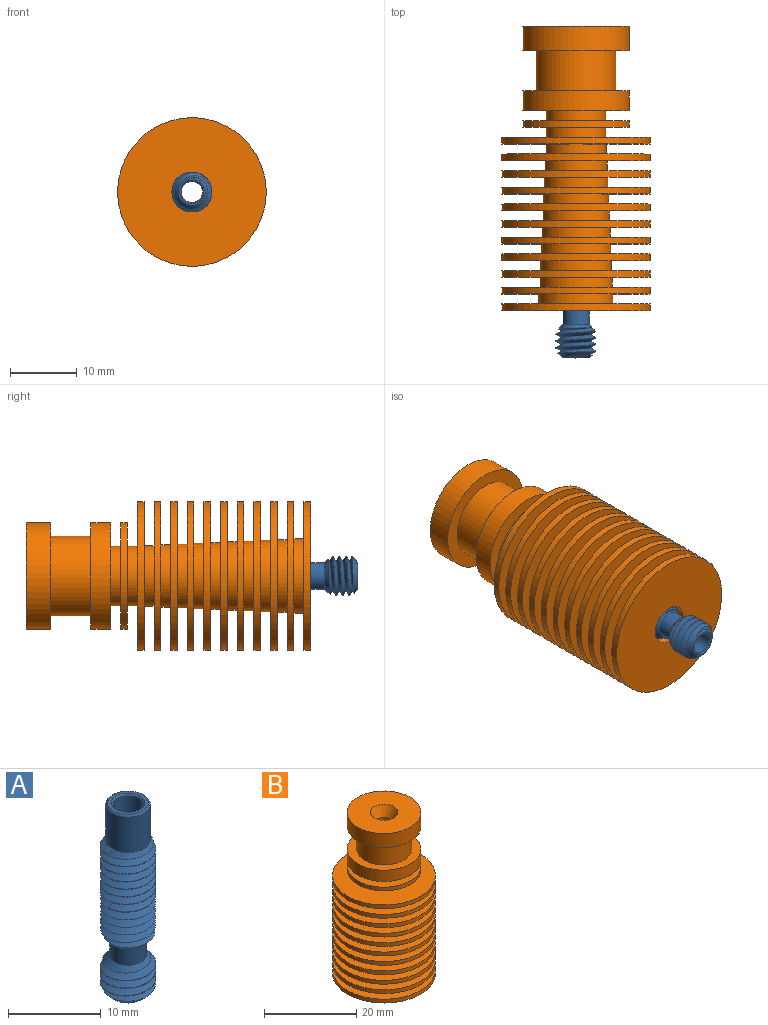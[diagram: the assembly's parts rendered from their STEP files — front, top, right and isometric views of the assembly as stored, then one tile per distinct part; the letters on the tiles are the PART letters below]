
ASSEMBLY  parts=2 mates=1
PART A: 23 faces, bbox 6x6.9x25.5 mm
  f0: cylinder r=2.4mm len=4.8mm, axis (0,0,1), area 70.9mm2, adj f11,f12,f13,f22
  f1: cylinder r=3mm len=7mm, axis (0,0,1), area 13.5mm2, adj f11,f13,f14,f17
  f2: cylinder r=3mm len=6mm, axis (0,0,1), area 4.2mm2, adj f7,f9,f18,f19
  f3: cylinder r=1.6mm len=24.7mm, axis (0,0,1), area 248.3mm2, adj f20,f21
  f4: plane 4.4x4.4mm, normal (0,0,1), area 5mm2, adj f21,f22
  f5: cylinder r=2mm len=4mm, axis (0,0,1), area 26.4mm2, adj f8,f10
  f6: plane 4x4mm, normal (0,0,-1), area 2.4mm2, adj f7,f20
  f7: cone r=3mm half-angle=45deg, axis (0,0,1), area 13.2mm2, adj f2,f6,f18,f19
  f8: cone r=2mm half-angle=45deg, axis (0,0,-1), area 13.1mm2, adj f5,f9,f18,f19
  f9: cone r=2mm half-angle=45deg, axis (0,0,-1), area 0.2mm2, adj f2,f8,f18
  f10: cone r=3mm half-angle=45deg, axis (0,0,1), area 11.5mm2, adj f5,f13,f14,f15,f16
  f11: cone r=2mm half-angle=45deg, axis (0,0,-1), area 6.7mm2, adj f0,f1,f12,f13,f14
  f12: plane 0.62x0.47mm, normal (0,1,0), area 0.1mm2, adj f0,f11,f13,f14
  f13: bspline ~13.63x6.93mm, area 182.7mm2, adj f0,f1,f10,f11,f12,f14,f16,f17
  f14: bspline ~13.46x6.93mm, area 114.4mm2, adj f1,f10,f11,f12,f13,f15,f17
  f15: bspline ~6.93x6.46mm, area 8.1mm2, adj f10,f14,f16,f17
  f16: bspline ~6.93x6.46mm, area 74.7mm2, adj f10,f13,f15,f17
  f17: plane 0.8x0.5mm, normal (0,1,0), area 0.1mm2, adj f1,f13,f14,f15,f16
  f18: bspline ~6.93x6mm, area 56.9mm2, adj f2,f7,f8,f9,f19
  f19: bspline ~6.93x6mm, area 56.8mm2, adj f2,f7,f8,f18
  f20: cone r=1.8mm half-angle=45deg, axis (0,0,-1), area 3mm2, adj f3,f6
  f21: cone r=1.6mm half-angle=45deg, axis (0,0,1), area 3mm2, adj f3,f4
  f22: cone r=2.2mm half-angle=45deg, axis (0,0,-1), area 4.1mm2, adj f0,f4
PART B: 59 faces, bbox 22.3x22.3x42.7 mm
  f0: cone r=1.6mm half-angle=70deg, axis (0,0,-1), area 21.5mm2, adj f1,f58
  f1: cylinder r=3mm len=18mm, axis (0,0,1), area 339.3mm2, adj f0,f2
  f2: plane 22.3x22.3mm, normal (0,0,-1), area 362.3mm2, adj f1,f3
  f3: cylinder r=11.15mm len=22.3mm, axis (0,0,1), area 70.1mm2, adj f2,f4
  f4: plane 22.3x22.3mm, normal (0,0,1), area 293.6mm2, adj f3,f5
  f5: cylinder r=5.56mm len=11.11mm, axis (0,0,1), area 52.4mm2, adj f4,f6
  f6: plane 22.3x22.3mm, normal (0,0,-1), area 293.6mm2, adj f5,f7
  f7: cylinder r=11.15mm len=22.3mm, axis (0,0,1), area 70.1mm2, adj f6,f8
  f8: plane 22.3x22.3mm, normal (0,0,1), area 297.4mm2, adj f7,f9
  f9: cylinder r=5.45mm len=10.89mm, axis (0,0,1), area 51.3mm2, adj f8,f10
  f10: plane 22.3x22.3mm, normal (0,0,-1), area 297.4mm2, adj f9,f11
  f11: cylinder r=11.15mm len=22.3mm, axis (0,0,1), area 70.1mm2, adj f10,f12
  f12: plane 22.3x22.3mm, normal (0,0,1), area 301.1mm2, adj f11,f13
  f13: cylinder r=5.34mm len=10.68mm, axis (0,0,1), area 50.3mm2, adj f12,f14
  f14: plane 22.3x22.3mm, normal (0,0,-1), area 301.1mm2, adj f13,f15
  f15: cylinder r=11.15mm len=22.3mm, axis (0,0,1), area 70.1mm2, adj f14,f16
  f16: plane 22.3x22.3mm, normal (0,0,1), area 304.7mm2, adj f15,f17
  f17: cylinder r=5.23mm len=10.46mm, axis (0,0,1), area 49.3mm2, adj f16,f18
  f18: plane 22.3x22.3mm, normal (0,0,-1), area 304.7mm2, adj f17,f19
  f19: cylinder r=11.15mm len=22.3mm, axis (0,0,1), area 70.1mm2, adj f18,f20
  f20: plane 22.3x22.3mm, normal (0,0,1), area 308.2mm2, adj f19,f21
  f21: cylinder r=5.12mm len=10.24mm, axis (0,0,1), area 48.3mm2, adj f20,f22
  f22: plane 22.3x22.3mm, normal (0,0,-1), area 308.2mm2, adj f21,f23
  f23: cylinder r=11.15mm len=22.3mm, axis (0,0,1), area 70.1mm2, adj f22,f24
  f24: plane 22.3x22.3mm, normal (0,0,1), area 311.7mm2, adj f23,f25
  f25: cylinder r=5.01mm len=10.02mm, axis (0,0,1), area 47.2mm2, adj f24,f26
  f26: plane 22.3x22.3mm, normal (0,0,-1), area 311.7mm2, adj f25,f27
  f27: cylinder r=11.15mm len=22.3mm, axis (0,0,1), area 70.1mm2, adj f26,f28
  f28: plane 22.3x22.3mm, normal (0,0,1), area 315.1mm2, adj f27,f29
  f29: cylinder r=4.9mm len=9.8mm, axis (0,0,1), area 46.2mm2, adj f28,f30
  f30: plane 22.3x22.3mm, normal (0,0,-1), area 315.1mm2, adj f29,f31
  f31: cylinder r=11.15mm len=22.3mm, axis (0,0,1), area 70.1mm2, adj f30,f32
  f32: plane 22.3x22.3mm, normal (0,0,1), area 318.4mm2, adj f31,f33
  f33: cylinder r=4.79mm len=9.58mm, axis (0,0,1), area 45.2mm2, adj f32,f34
  f34: plane 22.3x22.3mm, normal (0,0,-1), area 318.4mm2, adj f33,f35
  f35: cylinder r=11.15mm len=22.3mm, axis (0,0,1), area 70.1mm2, adj f34,f36
  f36: plane 22.3x22.3mm, normal (0,0,1), area 321.7mm2, adj f35,f37
  f37: cylinder r=4.68mm len=9.37mm, axis (0,0,1), area 44.1mm2, adj f36,f38
  f38: plane 22.3x22.3mm, normal (0,0,-1), area 321.7mm2, adj f37,f39
  f39: cylinder r=11.15mm len=22.3mm, axis (0,0,1), area 70.1mm2, adj f38,f40
  f40: plane 22.3x22.3mm, normal (0,0,1), area 324.8mm2, adj f39,f41
  f41: cylinder r=4.57mm len=9.15mm, axis (0,0,1), area 43.1mm2, adj f40,f42
  f42: plane 22.3x22.3mm, normal (0,0,-1), area 324.8mm2, adj f41,f43
  f43: cylinder r=11.15mm len=22.3mm, axis (0,0,1), area 70.1mm2, adj f42,f44
  f44: plane 22.3x22.3mm, normal (0,0,1), area 327.9mm2, adj f43,f45
  f45: cylinder r=4.46mm len=8.93mm, axis (0,0,1), area 42.1mm2, adj f44,f46
  f46: plane 16x16mm, normal (0,0,-1), area 138.4mm2, adj f45,f47
  f47: cylinder r=8mm len=16mm, axis (0,0,1), area 50.3mm2, adj f46,f48
  f48: plane 16x16mm, normal (0,0,1), area 138.4mm2, adj f47,f49
  f49: cylinder r=4.46mm len=8.93mm, axis (0,0,1), area 42.1mm2, adj f48,f50
  f50: plane 16x16mm, normal (0,0,-1), area 138.4mm2, adj f49,f51
  f51: cylinder r=8mm len=16mm, axis (0,0,1), area 150.8mm2, adj f50,f52
  f52: plane 16x16mm, normal (0,0,1), area 88mm2, adj f51,f53
  f53: cylinder r=6mm len=12mm, axis (0,0,1), area 226.2mm2, adj f52,f54
  f54: plane 16x16mm, normal (0,0,-1), area 88mm2, adj f53,f55
  f55: cylinder r=8mm len=16mm, axis (0,0,1), area 186mm2, adj f54,f56
  f56: plane 16x16mm, normal (0,0,1), area 172.8mm2, adj f55,f57
  f57: cone r=3mm half-angle=30deg, axis (0,0,1), area 40.5mm2, adj f56,f58
  f58: cylinder r=1.6mm len=21.77mm, axis (0,0,1), area 218.8mm2, adj f0,f57
PLACE A rot(axis=(-1,0,0),90deg) t=(77.22,-33.87,-12.84)mm
PLACE B rot(axis=(-1,0,0),90deg) t=(77.22,-26.77,-12.84)mm
MATE cylindrical A.f0 <-> B.f1  axis (0,1,0) through (77.22,-26.77,-12.84)mm
